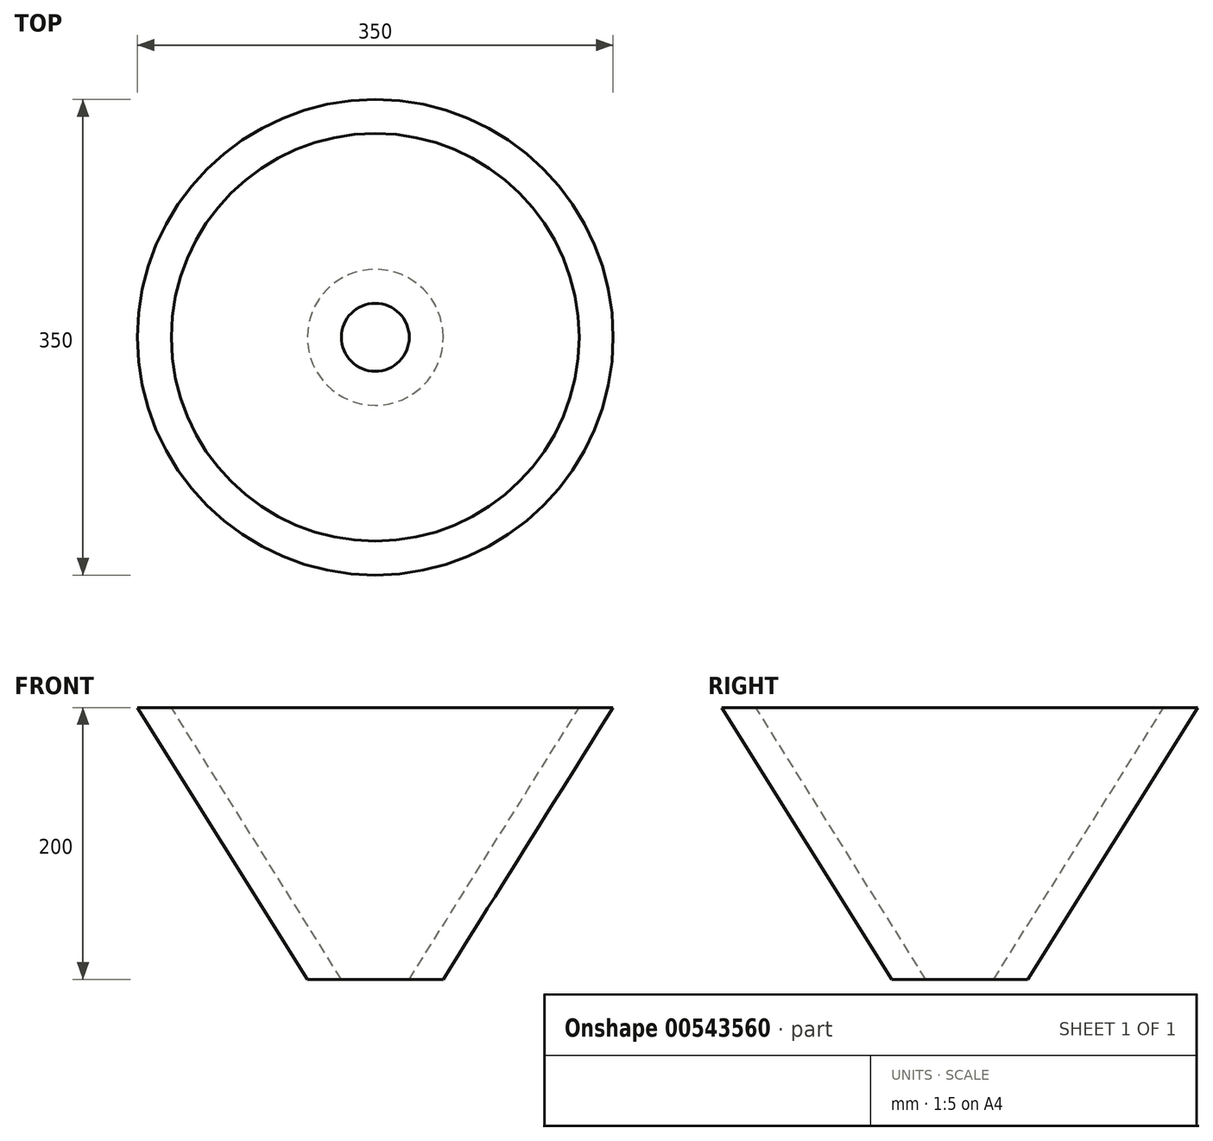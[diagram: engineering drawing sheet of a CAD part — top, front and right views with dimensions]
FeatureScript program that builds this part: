
annotation { "Feature Type Name" : "Feature", "Feature Type Description" : "" }
export const myFeature = defineFeature(function(context is Context, id is Id, definition is map)
    precondition{}
    {
        {
            var Q0;
            Q0=qCreatedBy(makeId("Front.planeOp"),FACE);
            var sketch = newSketch(context, id + "F0", { "sketchPlane" : qUnion([Q0])});
            skLineSegment(sketch, "E0", {"start": v(0, 101.74) * mm, "end": v(0, -98.26) * mm});
            skLineSegment(sketch, "E1", {"start": v(150, 101.74) * mm, "end": v(175, 101.74) * mm});
            skLineSegment(sketch, "E2", {"start": v(175, 101.74) * mm, "end": v(50, -98.26) * mm});
            skLineSegment(sketch, "E3", {"start": v(50, -98.26) * mm, "end": v(50, -98.26) * mm});
            skLineSegment(sketch, "E4", {"start": v(50, -98.26) * mm, "end": v(25, -98.26) * mm});
            skLineSegment(sketch, "E5", {"start": v(150, 101.74) * mm, "end": v(25, -98.26) * mm});
            skSolve(sketch);
        }
        {
            var Q0;
            Q0 = qSketchRegion(id + "F0", true);
            var Q1;
            Q1=sQuery(id+"F0.wireOp",EDGE,"E0");
            revolve(context, id + "F1", {"entities" : qUnion([Q0]), "axis" : qUnion([Q1]), "revolveType" : RevolveType.FULL});
        }
    });
